FCSTD DOCUMENT  (FreeCAD 1.1R41365 (Git))
Label: Assembly_WireFlexureUnit
License: All rights reserved
LicenseURL: https://en.wikipedia.org/wiki/All_rights_reserved
objects: App::FeaturePython×24, App::Link×16, App::Point×1, Assembly::JointGroup×1, Assembly::AssemblyObject×1
EXTERNAL_REF file=WireFlexure.FCStd obj=Body
EXTERNAL_REF file=BallJointMount.FCStd obj=Body
EXTERNAL_REF file=JointBall.FCStd obj=Body
EXTERNAL_REF file=RubberBandCollet.FCStd obj=Body
EXTERNAL_REF file=RubberBand.FCStd obj=Body

FEATURE [App::Point] Origin001
  Role = Origin
FEATURE [App::Link] FlexureWire  label="FlexureWire1"
  LinkPlacement = pos=(-8.5,9.53674e-07,0) rot=(0,0,1;0rad)
  LinkedObject = -> <external WireFlexure.FCStd>#Body
  Placement = pos=(-8.5,9.53674e-07,0) rot=(0,0,1;0rad)
FEATURE [App::FeaturePython] GroundedJoint  # Assembly grounded joint (typed FeaturePython)
  ObjectToGround = -> FlexureWire
FEATURE [App::Link] FlexureWire001  label="FlexureWire2"
  LinkPlacement = pos=(8.5,-9.53675e-07,0) rot=(0,0,1;0rad)
  LinkedObject = -> <external WireFlexure.FCStd>#Body
  Placement = pos=(8.5,-9.53675e-07,0) rot=(0,0,1;0rad)
FEATURE [App::Link] WireMount  label="WireMount1"
  LinkPlacement = pos=(1.421e-13,40,0) rot=(0,0,1;0rad)
  LinkedObject = -> <external BallJointMount.FCStd>#Body
  Placement = pos=(1.421e-13,40,0) rot=(0,0,1;0rad)
FEATURE [App::Link] WireMount001  label="WireMount2"
  LinkPlacement = pos=(3.73908e-06,-40,0) rot=(1,0,0;3.14159rad)
  LinkedObject = -> <external BallJointMount.FCStd>#Body
  Placement = pos=(3.73908e-06,-40,0) rot=(1,0,0;3.14159rad)
FEATURE [App::Link] Ball  label="Ball1"
  LinkPlacement = pos=(-8.5,36.5,0) rot=(0,0,1;0rad)
  LinkedObject = -> <external JointBall.FCStd>#Body
  Placement = pos=(-8.5,36.5,0) rot=(0,0,1;0rad)
FEATURE [App::Link] Ball001  label="Ball2"
  LinkPlacement = pos=(8.5,36.5,0) rot=(0,0,1;0rad)
  LinkedObject = -> <external JointBall.FCStd>#Body
  Placement = pos=(8.5,36.5,0) rot=(0,0,1;0rad)
FEATURE [App::Link] Ball002  label="Ball3"
  LinkPlacement = pos=(-8.5,-36.5,0) rot=(0,0,1;0rad)
  LinkedObject = -> <external JointBall.FCStd>#Body
  Placement = pos=(-8.5,-36.5,0) rot=(0,0,1;0rad)
FEATURE [App::Link] Ball003  label="Ball4"
  LinkPlacement = pos=(8.5,-36.5,0) rot=(0,0,1;0rad)
  LinkedObject = -> <external JointBall.FCStd>#Body
  Placement = pos=(8.5,-36.5,0) rot=(0,0,1;0rad)
FEATURE [App::FeaturePython] GroundedJoint001  # Assembly grounded joint (typed FeaturePython)
  ObjectToGround = -> FlexureWire001
FEATURE [App::FeaturePython] GroundedJoint002  # Assembly grounded joint (typed FeaturePython)
  ObjectToGround = -> WireMount
FEATURE [App::FeaturePython] GroundedJoint003  # Assembly grounded joint (typed FeaturePython)
  ObjectToGround = -> WireMount001
FEATURE [App::FeaturePython] GroundedJoint004  # Assembly grounded joint (typed FeaturePython)
  ObjectToGround = -> Ball
FEATURE [App::FeaturePython] GroundedJoint005  # Assembly grounded joint (typed FeaturePython)
  ObjectToGround = -> Ball001
FEATURE [App::FeaturePython] GroundedJoint006  # Assembly grounded joint (typed FeaturePython)
  ObjectToGround = -> Ball002
FEATURE [App::FeaturePython] GroundedJoint007  # Assembly grounded joint (typed FeaturePython)
  ObjectToGround = -> Ball003
FEATURE [App::Link] RubberBandCollet
  LinkPlacement = pos=(-8.5,-24,-1.04e-14) rot=(1,0,0;1.5708rad)
  LinkedObject = -> <external RubberBandCollet.FCStd>#Body
  Placement = pos=(-8.5,-24,-1.04e-14) rot=(1,0,0;1.5708rad)
FEATURE [App::Link] RubberBandCollet001
  LinkPlacement = pos=(8.5,-24,-1.04e-14) rot=(1,0,0;1.5708rad)
  LinkedObject = -> <external RubberBandCollet.FCStd>#Body
  Placement = pos=(8.5,-24,-1.04e-14) rot=(1,0,0;1.5708rad)
FEATURE [App::Link] RubberBandCollet002
  LinkPlacement = pos=(-8.5,24,-5.5e-15) rot=(1,0,0;4.71239rad)
  LinkedObject = -> <external RubberBandCollet.FCStd>#Body
  Placement = pos=(-8.5,24,-5.5e-15) rot=(1,0,0;4.71239rad)
FEATURE [App::Link] RubberBandCollet003
  LinkPlacement = pos=(8.5,24,-5.5e-15) rot=(1,0,0;4.71239rad)
  LinkedObject = -> <external RubberBandCollet.FCStd>#Body
  Placement = pos=(8.5,24,-5.5e-15) rot=(1,0,0;4.71239rad)
FEATURE [App::Link] RubberBand
  LinkPlacement = pos=(-8.5,-44,-2.22928e-06) rot=(0,1,0;1.5708rad)
  LinkedObject = -> <external RubberBand.FCStd>#Body
  Placement = pos=(-8.5,-44,-2.22928e-06) rot=(0,1,0;1.5708rad)
FEATURE [App::Link] RubberBand001
  LinkPlacement = pos=(8.5,-44,2.22928e-06) rot=(0,1,0;1.5708rad)
  LinkedObject = -> <external RubberBand.FCStd>#Body
  Placement = pos=(8.5,-44,2.22928e-06) rot=(0,1,0;1.5708rad)
FEATURE [App::Link] RubberBand002
  LinkPlacement = pos=(8.5,44,7e-16) rot=(0.707107,0,-0.707107;3.14159rad)
  LinkedObject = -> <external RubberBand.FCStd>#Body
  Placement = pos=(8.5,44,7e-16) rot=(0.707107,0,-0.707107;3.14159rad)
FEATURE [App::Link] RubberBand003
  LinkPlacement = pos=(-8.5,44,-1.4e-15) rot=(-0.707107,0,0.707107;3.14159rad)
  LinkedObject = -> <external RubberBand.FCStd>#Body
  Placement = pos=(-8.5,44,-1.4e-15) rot=(-0.707107,0,0.707107;3.14159rad)
FEATURE [App::FeaturePython] Joint  label="Fixed002"  # Assembly joint (typed FeaturePython)
  Activated = true
  Angle = 0
  AngleMax = 0
  AngleMin = 0
  Detach1 = false
  Detach2 = false
  Distance = 0
  Distance2 = 0
  EnableAngleMax = false
  EnableAngleMin = false
  EnableLengthMax = false
  EnableLengthMin = false
  JointType = 0 (Fixed)
  LengthMax = 0
  LengthMin = 0
  Offset2 = pos=(0,0,-8) rot=(0,0,1;0rad)
  Placement1 = pos=(0,0,3) rot=(0,0,1;0rad)
  Placement2 = pos=(0,-27,-9.8e-15) rot=(1,0,0;1.5708rad)
  Reference1 = -> Assembly [RubberBandCollet.Face20,RubberBandCollet.Edge3]
  Reference2 = -> Assembly [FlexureWire.Face1,FlexureWire.Edge3]
  Suppressed = false
FEATURE [App::FeaturePython] Joint001  label="Fixed"  # Assembly joint (typed FeaturePython)
  Activated = true
  Angle = 0
  AngleMax = 0
  AngleMin = 0
  Detach1 = false
  Detach2 = false
  Distance = 0
  Distance2 = 0
  EnableAngleMax = false
  EnableAngleMin = false
  EnableLengthMax = false
  EnableLengthMin = false
  JointType = 0 (Fixed)
  LengthMax = 0
  LengthMin = 0
  Offset2 = pos=(0,0,-8) rot=(0,0,1;0rad)
  Placement1 = pos=(0,0,3) rot=(0,0,1;0rad)
  Placement2 = pos=(0,-27,-9.8e-15) rot=(1,0,0;1.5708rad)
  Reference1 = -> Assembly [RubberBandCollet001.Edge27,RubberBandCollet001.Edge27]
  Reference2 = -> Assembly [FlexureWire001.Face1,FlexureWire001.Edge3]
  Suppressed = false
FEATURE [App::FeaturePython] Joint002  label="Fixed003"  # Assembly joint (typed FeaturePython)
  Activated = true
  Angle = 0
  AngleMax = 0
  AngleMin = 0
  Detach1 = false
  Detach2 = false
  Distance = 0
  Distance2 = 0
  EnableAngleMax = false
  EnableAngleMin = false
  EnableLengthMax = false
  EnableLengthMin = false
  JointType = 0 (Fixed)
  LengthMax = 0
  LengthMin = 0
  Offset2 = pos=(0,0,8) rot=(0,0,1;0rad)
  Placement1 = pos=(0,0,3) rot=(0,0,1;0rad)
  Placement2 = pos=(0,27,-6.2e-15) rot=(1,0,0;1.5708rad)
  Reference1 = -> Assembly [RubberBandCollet002.Edge27,RubberBandCollet002.Edge27]
  Reference2 = -> Assembly [FlexureWire.Face1,FlexureWire.Edge2]
  Suppressed = false
FEATURE [App::FeaturePython] Joint003  label="Fixed005"  # Assembly joint (typed FeaturePython)
  Activated = true
  Angle = 0
  AngleMax = 0
  AngleMin = 0
  Detach1 = false
  Detach2 = false
  Distance = 0
  Distance2 = 0
  EnableAngleMax = false
  EnableAngleMin = false
  EnableLengthMax = false
  EnableLengthMin = false
  JointType = 0 (Fixed)
  LengthMax = 0
  LengthMin = 0
  Offset2 = pos=(0,0,8) rot=(0,0,1;0rad)
  Placement1 = pos=(0,0,3) rot=(0,0,1;0rad)
  Placement2 = pos=(0,27,-6.2e-15) rot=(1,0,0;1.5708rad)
  Reference1 = -> Assembly [RubberBandCollet003.Edge27,RubberBandCollet003.Edge27]
  Reference2 = -> Assembly [FlexureWire001.Face1,FlexureWire001.Edge2]
  Suppressed = false
FEATURE [App::FeaturePython] Joint004  label="Cylindrical009"  # Assembly joint (typed FeaturePython)
  Activated = true
  Angle = 0
  AngleMax = 0
  AngleMin = 0
  Detach1 = false
  Detach2 = false
  Distance = 0
  Distance2 = 0
  EnableAngleMax = false
  EnableAngleMin = false
  EnableLengthMax = false
  EnableLengthMin = false
  JointType = 2 (Cylindrical)
  LengthMax = 0
  LengthMin = 0
  Placement1 = pos=(-1.75,0,0) rot=(1,0,0;1.5708rad)
  Placement2 = pos=(-8.5,3,-1.75) rot=(-1,0,0;4.71239rad)
  Reference1 = -> Assembly [RubberBand.Edge1,RubberBand.Edge1]
  Reference2 = -> Assembly [WireMount001.Edge38,WireMount001.Edge38]
  Suppressed = false
FEATURE [App::FeaturePython] Joint005  label="Cylindrical010"  # Assembly joint (typed FeaturePython)
  Activated = true
  Angle = 0
  AngleMax = 0
  AngleMin = 0
  Detach1 = false
  Detach2 = false
  Distance = 0
  Distance2 = 0
  EnableAngleMax = false
  EnableAngleMin = false
  EnableLengthMax = false
  EnableLengthMin = false
  JointType = 2 (Cylindrical)
  LengthMax = 0
  LengthMin = 0
  Placement1 = pos=(1.75,7.1e-15,0) rot=(0,-0.707107,0.707107;3.14159rad)
  Placement2 = pos=(-8.5,3,1.75) rot=(-1,0,0;4.71239rad)
  Reference1 = -> Assembly [RubberBand.Face5,RubberBand.Edge2]
  Reference2 = -> Assembly [WireMount001.Edge37,WireMount001.Edge37]
  Suppressed = false
FEATURE [App::FeaturePython] Joint006  label="Distance007"  # Assembly joint (typed FeaturePython)
  Activated = true
  Angle = 0
  AngleMax = 0
  AngleMin = 0
  Detach1 = false
  Detach2 = false
  Distance = -1
  Distance2 = 0
  EnableAngleMax = false
  EnableAngleMin = false
  EnableLengthMax = false
  EnableLengthMin = false
  JointType = 5 (Distance)
  LengthMax = 0
  LengthMin = 0
  Placement1 = pos=(-1.75,0,0) rot=(0.57735,0.57735,-0.57735;2.0944rad)
  Placement2 = pos=(2.1e-15,3,8e-16) rot=(-0.57735,-0.57735,-0.57735;2.0944rad)
  Reference1 = -> Assembly [RubberBand.Face1,RubberBand.Face1]
  Reference2 = -> Assembly [WireMount001.Face12,WireMount001.Vertex27]
  Suppressed = false
FEATURE [App::FeaturePython] Joint007  label="Cylindrical011"  # Assembly joint (typed FeaturePython)
  Activated = true
  Angle = 0
  AngleMax = 0
  AngleMin = 0
  Detach1 = false
  Detach2 = false
  Distance = 0
  Distance2 = 0
  EnableAngleMax = false
  EnableAngleMin = false
  EnableLengthMax = false
  EnableLengthMin = false
  JointType = 2 (Cylindrical)
  LengthMax = 0
  LengthMin = 0
  Placement1 = pos=(-1.75,-7.1e-15,0) rot=(1,0,0;1.5708rad)
  Placement2 = pos=(8.5,3,-1.75) rot=(0,-0.707107,-0.707107;3.14159rad)
  Reference1 = -> Assembly [RubberBand001.Edge1,RubberBand001.Edge1]
  Reference2 = -> Assembly [WireMount001.Edge40,WireMount001.Edge40]
  Suppressed = false
FEATURE [App::FeaturePython] Joint008  label="Cylindrical012"  # Assembly joint (typed FeaturePython)
  Activated = true
  Angle = 0
  AngleMax = 0
  AngleMin = 0
  Detach1 = false
  Detach2 = false
  Distance = 0
  Distance2 = 0
  EnableAngleMax = false
  EnableAngleMin = false
  EnableLengthMax = false
  EnableLengthMin = false
  JointType = 2 (Cylindrical)
  LengthMax = 0
  LengthMin = 0
  Placement1 = pos=(1.75,0,0) rot=(0,-0.707107,0.707107;3.14159rad)
  Placement2 = pos=(8.5,3,1.75) rot=(0,-0.707107,-0.707107;3.14159rad)
  Reference1 = -> Assembly [RubberBand001.Face5,RubberBand001.Edge2]
  Reference2 = -> Assembly [WireMount001.Face27,WireMount001.Edge3]
  Suppressed = false
FEATURE [App::FeaturePython] Joint009  label="Distance009"  # Assembly joint (typed FeaturePython)
  Activated = true
  Angle = 0
  AngleMax = 0
  AngleMin = 0
  Detach1 = false
  Detach2 = false
  Distance = -1
  Distance2 = 0
  EnableAngleMax = false
  EnableAngleMin = false
  EnableLengthMax = false
  EnableLengthMin = false
  JointType = 5 (Distance)
  LengthMax = 0
  LengthMin = 0
  Placement1 = pos=(-1.75,-7.1e-15,0) rot=(0.57735,0.57735,-0.57735;2.0944rad)
  Placement2 = pos=(2.1e-15,3,8e-16) rot=(-0.57735,-0.57735,-0.57735;2.0944rad)
  Reference1 = -> Assembly [RubberBand001.Face1,RubberBand001.Face1]
  Reference2 = -> Assembly [WireMount001.Face12,WireMount001.Vertex29]
  Suppressed = false
FEATURE [App::FeaturePython] Joint010  label="Cylindrical013"  # Assembly joint (typed FeaturePython)
  Activated = true
  Angle = 0
  AngleMax = 0
  AngleMin = 0
  Detach1 = false
  Detach2 = false
  Distance = 0
  Distance2 = 0
  EnableAngleMax = false
  EnableAngleMin = false
  EnableLengthMax = false
  EnableLengthMin = false
  JointType = 2 (Cylindrical)
  LengthMax = 0
  LengthMin = 0
  Placement1 = pos=(-1.75,0,0) rot=(1,0,0;1.5708rad)
  Placement2 = pos=(-8.5,3,1.75) rot=(1,0,0;1.5708rad)
  Reference1 = -> Assembly [RubberBand003.Edge1,RubberBand003.Edge1]
  Reference2 = -> Assembly [WireMount.Edge37,WireMount.Edge37]
  Suppressed = false
FEATURE [App::FeaturePython] Joint011  label="Cylindrical014"  # Assembly joint (typed FeaturePython)
  Activated = true
  Angle = 0
  AngleMax = 0
  AngleMin = 0
  Detach1 = false
  Detach2 = false
  Distance = 0
  Distance2 = 0
  EnableAngleMax = false
  EnableAngleMin = false
  EnableLengthMax = false
  EnableLengthMin = false
  JointType = 2 (Cylindrical)
  LengthMax = 0
  LengthMin = 0
  Placement1 = pos=(1.75,0,0) rot=(0,0.707107,-0.707107;3.14159rad)
  Placement2 = pos=(-8.5,3,-1.75) rot=(1,0,0;1.5708rad)
  Reference1 = -> Assembly [RubberBand003.Face5,RubberBand003.Edge2]
  Reference2 = -> Assembly [WireMount.Face26,WireMount.Edge3]
  Suppressed = false
FEATURE [App::FeaturePython] Joint012  label="Distance010"  # Assembly joint (typed FeaturePython)
  Activated = true
  Angle = 0
  AngleMax = 0
  AngleMin = 0
  Detach1 = false
  Detach2 = false
  Distance = -1
  Distance2 = 0
  EnableAngleMax = false
  EnableAngleMin = false
  EnableLengthMax = false
  EnableLengthMin = false
  JointType = 5 (Distance)
  LengthMax = 0
  LengthMin = 0
  Placement1 = pos=(-1.75,0,0) rot=(0.57735,0.57735,-0.57735;2.0944rad)
  Placement2 = pos=(1.5e-15,3,8e-16) rot=(0.57735,0.57735,0.57735;4.18879rad)
  Reference1 = -> Assembly [RubberBand003.Face1,RubberBand003.Face1]
  Reference2 = -> Assembly [WireMount.Face12,WireMount.Vertex26]
  Suppressed = false
FEATURE [App::FeaturePython] Joint013  label="Cylindrical015"  # Assembly joint (typed FeaturePython)
  Activated = true
  Angle = 0
  AngleMax = 0
  AngleMin = 0
  Detach1 = false
  Detach2 = false
  Distance = 0
  Distance2 = 0
  EnableAngleMax = false
  EnableAngleMin = false
  EnableLengthMax = false
  EnableLengthMin = false
  JointType = 2 (Cylindrical)
  LengthMax = 0
  LengthMin = 0
  Placement1 = pos=(-1.75,0,0) rot=(1,0,0;1.5708rad)
  Placement2 = pos=(8.5,3,1.75) rot=(0,0.707107,0.707107;3.14159rad)
  Reference1 = -> Assembly [RubberBand002.Edge1,RubberBand002.Edge1]
  Reference2 = -> Assembly [WireMount.Edge39,WireMount.Edge39]
  Suppressed = false
FEATURE [App::FeaturePython] Joint014  label="Cylindrical018"  # Assembly joint (typed FeaturePython)
  Activated = true
  Angle = 0
  AngleMax = 0
  AngleMin = 0
  Detach1 = false
  Detach2 = false
  Distance = 0
  Distance2 = 0
  EnableAngleMax = false
  EnableAngleMin = false
  EnableLengthMax = false
  EnableLengthMin = false
  JointType = 2 (Cylindrical)
  LengthMax = 0
  LengthMin = 0
  Placement1 = pos=(1.75,0,0) rot=(0,-0.707107,0.707107;3.14159rad)
  Placement2 = pos=(8.5,3,-1.75) rot=(0,0.707107,0.707107;3.14159rad)
  Reference1 = -> Assembly [RubberBand002.Face5,RubberBand002.Edge2]
  Reference2 = -> Assembly [WireMount.Face28,WireMount.Edge3]
  Suppressed = false
FEATURE [App::FeaturePython] Joint015  label="Distance014"  # Assembly joint (typed FeaturePython)
  Activated = true
  Angle = 0
  AngleMax = 0
  AngleMin = 0
  Detach1 = false
  Detach2 = false
  Distance = -1
  Distance2 = 0
  EnableAngleMax = false
  EnableAngleMin = false
  EnableLengthMax = false
  EnableLengthMin = false
  JointType = 5 (Distance)
  LengthMax = 0
  LengthMin = 0
  Placement1 = pos=(-1.75,0,0) rot=(-0.57735,-0.57735,0.57735;4.18879rad)
  Placement2 = pos=(1.5e-15,3,8e-16) rot=(0.57735,0.57735,0.57735;4.18879rad)
  Reference1 = -> Assembly [RubberBand002.Face1,RubberBand002.Face1]
  Reference2 = -> Assembly [WireMount.Face12,WireMount.Face12]
  Suppressed = false
FEATURE [Assembly::JointGroup] Joints
  Group = -> [GroundedJoint,GroundedJoint001,GroundedJoint002,GroundedJoint003,GroundedJoint004,GroundedJoint005,GroundedJoint006,GroundedJoint007,Joint,Joint001,Joint002,Joint003,Joint004,Joint005,Joint006,Joint007,Joint008,Joint009,Joint010,Joint011,Joint012,Joint013,Joint014,Joint015]
FEATURE [Assembly::AssemblyObject] Assembly  label="WireFlexureUnit"
  Group = -> [Joints,FlexureWire,GroundedJoint,FlexureWire001,WireMount,WireMount001,Ball,Ball001,Ball002,Ball003,GroundedJoint001,GroundedJoint002,GroundedJoint003,GroundedJoint004,GroundedJoint005,GroundedJoint006,GroundedJoint007,RubberBandCollet,RubberBandCollet001,RubberBandCollet002,RubberBandCollet003,RubberBand,RubberBand001,RubberBand002,RubberBand003,Joint,Joint001,Joint002,Joint003,Joint004,Joint005,+10 more]
  Origin = -> Origin
  Type = Assembly

RESOLVED EXTERNAL PARTS (link-assembly join: the EXTERNAL_REF files above that resolve inside this repo's crawl, each included once):
---- part BallJointMount.FCStd = doc fcstd_7bda6f26d7a0 ----
FCSTD DOCUMENT  (FreeCAD 1.1R41365 (Git))
Label: BallJointMount
License: All rights reserved
LicenseURL: https://en.wikipedia.org/wiki/All_rights_reserved
objects: Sketcher::SketchObject×4, PartDesign::Pocket×3, PartDesign::Chamfer×2, App::Point×1, PartDesign::Pad×1, PartDesign::Fillet×1, PartDesign::Mirrored×1, PartDesign::Body×1
note: 32 computed .brp shape members not serialized (recipe doc carries the construction recipe); baked Part::Feature solids carry a one-line shape summary decoded from their .brp

FEATURE [App::Point] Origin001
  Role = Origin
FEATURE [Sketcher::SketchObject] Sketch
  ArcFitTolerance = 1e-06
  AttachmentSupport = -> [XY_Plane]
  ExternalTypes = [0]
  FullyConstrained = true
  MakeInternals = false
  MapMode = 5
  sketch-geometry (5):
    g0: LineSegment StartX=-10 StartY=-3 StartZ=0 EndX=0 EndY=-3 EndZ=0
    g1: LineSegment StartX=0 StartY=-3 StartZ=0 EndX=0 EndY=3 EndZ=0
    g2: LineSegment StartX=0 StartY=3 StartZ=0 EndX=-10 EndY=3 EndZ=0
    g3: GeomPoint [constr] X=0 Y=0 Z=0
    g4: LineSegment StartX=-10 StartY=3 StartZ=0 EndX=-10 EndY=-3 EndZ=0
  constraints (12):
    c: Coincident(g0,g1)
    c: Coincident(g1,g2)
    c: Horizontal(g0)
    c: Horizontal(g2)
    c: Vertical(g1)
    c: Coincident(g3,g-1)
    c: DistanceX(g0,g0) = 10
    c: DistanceY(g1,g1) = 6
    c: Symmetric(g1,g1,g3)
    c: Coincident(g4,g2)
    c: Coincident(g4,g0)
    c: Vertical(g4)
FEATURE [PartDesign::Pad] Pad
  Direction = (0,0,1)
  Length = 6
  Length2 = 10
  Midplane = true
  Profile = -> Sketch
  ReferenceAxis = -> Sketch [N_Axis]
  Refine = true
  Suppressed = false
  Type = 0
FEATURE [Sketcher::SketchObject] Sketch001
  ArcFitTolerance = 1e-06
  AttachmentSupport = -> [Pad]
  ExternalTypes = [0]
  FullyConstrained = true
  MakeInternals = false
  MapMode = 5
  Placement = pos=(0,0,3) rot=(0,0,1;0rad)
  sketch-geometry (1):
    g0: Circle CenterX=-5 CenterY=0 CenterZ=0 NormalX=0 NormalY=0 NormalZ=1 AngleXU=0 Radius=1.1
  constraints (3):
    c: Diameter(g0) = 2.2
    c: DistanceX(g0,g-1) = 5
    c: PointOnObject(g0,g-1)
FEATURE [PartDesign::Pocket] Pocket
  BaseFeature = -> Pad
  Direction = (0,0,-1)
  Length = 5
  Length2 = 5
  Profile = -> Sketch001
  ReferenceAxis = -> Sketch001 [N_Axis]
  Refine = true
  Suppressed = false
  Type = 1
FEATURE [Sketcher::SketchObject] Sketch002
  ArcFitTolerance = 1e-06
  AttachmentSupport = -> [Pocket]
  ExternalTypes = [0]
  FullyConstrained = true
  MakeInternals = false
  MapMode = 5
  Placement = pos=(0,-3,0) rot=(1,0,0;1.5708rad)
  sketch-geometry (1):
    g0: Circle CenterX=-8.5 CenterY=0 CenterZ=0 NormalX=0 NormalY=0 NormalZ=1 AngleXU=0 Radius=0.5
  constraints (3):
    c: Diameter(g0) = 1
    c: DistanceX(g0,g-1) = 8.5
    c: PointOnObject(g0,g-1)
FEATURE [PartDesign::Pocket] Pocket001
  BaseFeature = -> Pocket
  Direction = (0,1,-2e-16)
  Length = 1
  Length2 = 5
  Profile = -> Sketch002
  ReferenceAxis = -> Sketch002 [N_Axis]
  Refine = true
  Suppressed = false
  Type = 0
FEATURE [PartDesign::Chamfer] Chamfer
  Angle = 45
  Base = -> Pocket001 [Edge14]
  BaseFeature = -> Pocket001
  ChamferType = 0
  FlipDirection = false
  Refine = true
  Size = 1.2
  Size2 = 1
  SupportTransform = false
  Suppressed = false
  UseAllEdges = false
FEATURE [Sketcher::SketchObject] Sketch004
  ArcFitTolerance = 1e-06
  AttachmentSupport = -> [Chamfer]
  ExternalGeometry = -> [Chamfer]
  ExternalTypes = [0]
  FullyConstrained = true
  MakeInternals = false
  MapMode = 5
  Placement = pos=(0,-3,0) rot=(1,0,0;1.5708rad)
  sketch-geometry (3):
    g0: Circle CenterX=-8.5 CenterY=1.75 CenterZ=0 NormalX=0 NormalY=0 NormalZ=1 AngleXU=0 Radius=0.6
    g1: Circle CenterX=-8.5 CenterY=-1.75 CenterZ=0 NormalX=0 NormalY=0 NormalZ=1 AngleXU=0 Radius=0.6
    g2: LineSegment [constr] StartX=-8.5 StartY=1.75 StartZ=0 EndX=-8.5 EndY=-1.75 EndZ=0
  constraints (7):
    c: Diameter(g0) = 1.2
    c: Equal(g0,g1)
    c: Coincident(g2,g0)
    c: Coincident(g2,g1)
    c: Symmetric(g2,g2,g-3)
    c: Distance(g2,g2) = 3.5
    c: Vertical(g2)
FEATURE [PartDesign::Pocket] Pocket002
  BaseFeature = -> Chamfer
  Direction = (0,1,-2e-16)
  Length = 5
  Length2 = 5
  Profile = -> Sketch004
  ReferenceAxis = -> Sketch004 [N_Axis]
  Refine = true
  Suppressed = false
  Type = 1
FEATURE [PartDesign::Fillet] Fillet
  Base = -> Pocket002 [Edge3,Edge15]
  BaseFeature = -> Pocket002
  Radius = 0.5
  Refine = true
  SupportTransform = false
  Suppressed = false
  UseAllEdges = false
FEATURE [PartDesign::Mirrored] Mirrored
  BaseFeature = -> Fillet
  MirrorPlane = -> YZ_Plane
  Refine = true
  Suppressed = false
  TransformMode = 1
FEATURE [PartDesign::Chamfer] Chamfer001
  Angle = 45
  Base = -> Mirrored [Edge5,Edge11]
  BaseFeature = -> Mirrored
  ChamferType = 0
  FlipDirection = false
  Refine = true
  Size = 0.2
  Size2 = 1
  SupportTransform = false
  Suppressed = false
  UseAllEdges = false
FEATURE [PartDesign::Body] Body  label="BallJointMount"
  AllowCompound = false
  Group = -> [Sketch,Pad,Sketch001,Pocket,Sketch002,Pocket001,Chamfer,Sketch004,Pocket002,Fillet,Mirrored,Chamfer001]
  Origin = -> Origin
  Tip = -> Chamfer001
---- part JointBall.FCStd = doc fcstd_40ae3ec74856 ----
FCSTD DOCUMENT  (FreeCAD 1.1R41365 (Git))
Label: JointBall
License: All rights reserved
LicenseURL: https://en.wikipedia.org/wiki/All_rights_reserved
objects: App::Point×1, Sketcher::SketchObject×1, PartDesign::Revolution×1, PartDesign::Body×1
note: 6 computed .brp shape members not serialized (recipe doc carries the construction recipe); baked Part::Feature solids carry a one-line shape summary decoded from their .brp

FEATURE [App::Point] Origin001
  Role = Origin
FEATURE [Sketcher::SketchObject] Sketch
  ArcFitTolerance = 1e-06
  AttachmentSupport = -> [Origin]
  ExternalTypes = [0]
  FullyConstrained = false
  MakeInternals = false
  MapMode = 5
  sketch-geometry (2):
    g0: ArcOfCircle CenterX=0.0245252 CenterY=-0.048148 CenterZ=0 NormalX=0 NormalY=0 NormalZ=1 AngleXU=0 Radius=0.75 StartAngle=0.0642415 EndAngle=3.07735
    g1: LineSegment StartX=-0.723928 StartY=0 StartZ=0 EndX=0.772978 EndY=0 EndZ=0
  constraints (5):
    c: Coincident(g1,g0)
    c: Coincident(g1,g0)
    c: Horizontal(g1)
    c: Radius(g0) = 0.75
    c: PointOnObject(g0,g-1)
FEATURE [PartDesign::Revolution] Revolution
  Angle = 360
  Angle2 = 60
  Axis = (1,0,0)
  Base = (0,0,0)
  Profile = -> Sketch
  ReferenceAxis = -> Sketch [H_Axis]
  Refine = true
  Suppressed = false
  Type = 0
FEATURE [PartDesign::Body] Body  label="Ball"
  AllowCompound = false
  Group = -> [Sketch,Revolution]
  Origin = -> Origin
  Tip = -> Revolution
---- part RubberBand.FCStd = doc fcstd_05857427589b ----
FCSTD DOCUMENT  (FreeCAD 1.1R41365 (Git))
Label: RubberBand
License: All rights reserved
LicenseURL: https://en.wikipedia.org/wiki/All_rights_reserved
objects: Sketcher::SketchObject×2, App::Point×1, PartDesign::AdditivePipe×1, PartDesign::Mirrored×1, PartDesign::Body×1
note: 10 computed .brp shape members not serialized (recipe doc carries the construction recipe); baked Part::Feature solids carry a one-line shape summary decoded from their .brp

FEATURE [App::Point] Origin001
  Role = Origin
FEATURE [Sketcher::SketchObject] Sketch
  ArcFitTolerance = 1e-06
  AttachmentSupport = -> [Origin]
  ExternalTypes = [0]
  FullyConstrained = true
  MakeInternals = false
  MapMode = 5
  sketch-geometry (2):
    g0: LineSegment StartX=-1.75 StartY=0 StartZ=0 EndX=-1.75 EndY=20 EndZ=0
    g1: ArcOfCircle CenterX=0 CenterY=20 CenterZ=0 NormalX=0 NormalY=0 NormalZ=1 AngleXU=0 Radius=1.75 StartAngle=1.5708 EndAngle=3.14159
  constraints (7):
    c: PointOnObject(g0,g-1)
    c: Vertical(g0)
    c: PointOnObject(g1,g-2)
    c: PointOnObject(g1,g-2)
    c: Tangent(g1,g0) = 1.5708
    c: Distance(g-1,g0) = 1.75
    c: DistanceY(g0,g0) = 20
FEATURE [Sketcher::SketchObject] Sketch001
  ArcFitTolerance = 1e-06
  AttachmentSupport = -> [Origin]
  ExternalGeometry = -> [Sketch]
  ExternalTypes = [0]
  FullyConstrained = true
  MakeInternals = false
  MapMode = 5
  Placement = pos=(0,0,0) rot=(1,0,0;1.5708rad)
  sketch-geometry (1):
    g0: Circle CenterX=-1.75 CenterY=0 CenterZ=0 NormalX=0 NormalY=0 NormalZ=1 AngleXU=0 Radius=0.5
  constraints (2):
    c: Diameter(g0) = 1
    c: Coincident(g0,g-3)
FEATURE [PartDesign::AdditivePipe] AdditivePipe
  AuxiliaryCurvilinear = true
  AuxiliarySpineTangent = false
  Binormal = (0,0,0)
  Mode = 0
  Profile = -> Sketch001
  Refine = true
  Spine = -> Sketch
  SpineTangent = false
  Suppressed = false
  Transformation = 0
  Transition = 0
FEATURE [PartDesign::Mirrored] Mirrored
  BaseFeature = -> AdditivePipe
  MirrorPlane = -> YZ_Plane
  Refine = true
  Suppressed = false
  TransformMode = 1
FEATURE [PartDesign::Body] Body  label="RubberBand"
  AllowCompound = false
  Group = -> [Sketch,Sketch001,AdditivePipe,Mirrored]
  Origin = -> Origin
  Tip = -> Mirrored
---- part RubberBandCollet.FCStd = doc fcstd_46be4b665b96 ----
FCSTD DOCUMENT  (FreeCAD 1.1R41365 (Git))
Label: RubberBandCollet
License: All rights reserved
LicenseURL: https://en.wikipedia.org/wiki/All_rights_reserved
objects: Sketcher::SketchObject×2, App::Point×1, PartDesign::Pad×1, PartDesign::Pocket×1, PartDesign::PolarPattern×1, PartDesign::Chamfer×1, PartDesign::Body×1
note: 16 computed .brp shape members not serialized (recipe doc carries the construction recipe); baked Part::Feature solids carry a one-line shape summary decoded from their .brp

FEATURE [App::Point] Origin001
  Role = Origin
FEATURE [Sketcher::SketchObject] Sketch
  ArcFitTolerance = 1e-06
  AttachmentSupport = -> [Origin]
  ExternalTypes = [0]
  FullyConstrained = true
  MakeInternals = false
  MapMode = 5
  sketch-geometry (8):
    g0: Circle CenterX=0 CenterY=0 CenterZ=0 NormalX=0 NormalY=0 NormalZ=1 AngleXU=0 Radius=1
    g1: ArcOfCircle CenterX=0 CenterY=1 CenterZ=0 NormalX=0 NormalY=0 NormalZ=1 AngleXU=0 Radius=2 StartAngle=2e-16 EndAngle=3.14159
    g2: ArcOfCircle CenterX=0 CenterY=-1 CenterZ=0 NormalX=0 NormalY=0 NormalZ=1 AngleXU=0 Radius=2 StartAngle=3.14159 EndAngle=6.28319
    g3: LineSegment StartX=2 StartY=1 StartZ=0 EndX=2 EndY=-1 EndZ=0
    g4: LineSegment StartX=-2 StartY=1 StartZ=0 EndX=-2 EndY=-1 EndZ=0
    g5: LineSegment [constr] StartX=0 StartY=1 StartZ=0 EndX=0 EndY=-1 EndZ=0
    g6: GeomPoint [constr] X=0 Y=-3 Z=0
    g7: GeomPoint [constr] X=0 Y=3 Z=0
  constraints (17):
    c: Coincident(g0,g-1)
    c: Diameter(g0) = 2
    c: Tangent(g1,g3) = 1.5708
    c: Tangent(g1,g4) = -1.5708
    c: Tangent(g2,g3) = 1.5708
    c: Tangent(g2,g4) = -1.5708
    c: Equal(g1,g2)
    c: Vertical(g4)
    c: Coincident(g5,g1)
    c: Coincident(g5,g2)
    c: Symmetric(g5,g5,g0)
    c: Distance(g3,g4) = 4
    c: PointOnObject(g6,g2)
    c: PointOnObject(g6,g-2)
    c: PointOnObject(g7,g1)
    c: PointOnObject(g7,g-2)
    c: DistanceY(g6,g7) = 6
FEATURE [PartDesign::Pad] Pad
  Direction = (0,0,1)
  Length = 3
  Length2 = 10
  Profile = -> Sketch
  ReferenceAxis = -> Sketch [N_Axis]
  Refine = true
  Suppressed = false
  Type = 0
FEATURE [Sketcher::SketchObject] Sketch001
  ArcFitTolerance = 1e-06
  AttachmentSupport = -> [Pad]
  ExternalTypes = [0]
  FullyConstrained = true
  MakeInternals = false
  MapMode = 5
  Placement = pos=(0,0,3) rot=(0,0,1;0rad)
  sketch-geometry (5):
    g0: ArcOfCircle CenterX=0 CenterY=2 CenterZ=0 NormalX=0 NormalY=0 NormalZ=1 AngleXU=0 Radius=0.5 StartAngle=2.41886 EndAngle=7.00592
    g1: GeomPoint [constr] X=0 Y=3 Z=0
    g2: LineSegment StartX=-0.375 StartY=2.33072 StartZ=0 EndX=-0.375 EndY=4.33072 EndZ=0
    g3: LineSegment StartX=-0.375 StartY=4.33072 StartZ=0 EndX=0.375 EndY=4.33072 EndZ=0
    g4: LineSegment StartX=0.375 StartY=4.33072 StartZ=0 EndX=0.375 EndY=2.33072 EndZ=0
  constraints (15):
    c: PointOnObject(g0,g-2)
    c: PointOnObject(g1,g-3)
    c: PointOnObject(g1,g-2)
    c: Vertical(g2)
    c: Horizontal(g3)
    c: Vertical(g4)
    c: Horizontal(g4,g2)
    c: Coincident(g2,g3)
    c: Coincident(g3,g4)
    c: DistanceX(g3,g3) = 0.75
    c: Diameter(g0) = 1
    c: Coincident(g2,g0)
    c: Coincident(g4,g0)
    c: DistanceY(g4,g4) = 2
    c: DistanceY(g-1,g0) = 2
FEATURE [PartDesign::Pocket] Pocket
  BaseFeature = -> Pad
  Direction = (0,0,-1)
  Length = 5
  Length2 = 5
  Profile = -> Sketch001
  ReferenceAxis = -> Sketch001 [N_Axis]
  Refine = true
  Suppressed = false
  Type = 1
FEATURE [PartDesign::PolarPattern] PolarPattern
  Angle = 360
  Axis = -> Z_Axis
  BaseFeature = -> Pocket
  Mode = 0
  Occurrences = 2
  Offset = 120
  Originals = -> [Pocket]
  Refine = true
  Suppressed = false
  TransformMode = 0
FEATURE [PartDesign::Chamfer] Chamfer
  Angle = 45
  Base = -> PolarPattern [Edge11,Edge25,Edge5,Edge19]
  BaseFeature = -> PolarPattern
  ChamferType = 0
  FlipDirection = false
  Refine = true
  Size = 0.4
  Size2 = 1
  SupportTransform = false
  Suppressed = false
  UseAllEdges = false
FEATURE [PartDesign::Body] Body  label="RubberBandCollet"
  AllowCompound = false
  Group = -> [Sketch,Pad,Sketch001,Pocket,PolarPattern,Chamfer]
  Origin = -> Origin
  Tip = -> Chamfer
---- part WireFlexure.FCStd = doc fcstd_6be79ddcf241 ----
FCSTD DOCUMENT  (FreeCAD 1.1R41365 (Git))
Label: WireFlexure
License: All rights reserved
LicenseURL: https://en.wikipedia.org/wiki/All_rights_reserved
objects: App::Point×1, Sketcher::SketchObject×1, PartDesign::Pad×1, PartDesign::Chamfer×1, PartDesign::Body×1
note: 9 computed .brp shape members not serialized (recipe doc carries the construction recipe); baked Part::Feature solids carry a one-line shape summary decoded from their .brp

FEATURE [App::Point] Origin001
  Role = Origin
FEATURE [Sketcher::SketchObject] Sketch
  ArcFitTolerance = 1e-06
  AttachmentSupport = -> [XZ_Plane]
  ExternalTypes = [0]
  FullyConstrained = true
  MakeInternals = false
  MapMode = 5
  Placement = pos=(0,0,0) rot=(1,0,0;1.5708rad)
  sketch-geometry (1):
    g0: Circle CenterX=0 CenterY=0 CenterZ=0 NormalX=0 NormalY=0 NormalZ=1 AngleXU=0 Radius=1
  constraints (2):
    c: Coincident(g0,g-1)
    c: Diameter(g0) = 2
FEATURE [PartDesign::Pad] Pad
  Direction = (0,-1,0)
  Length = 72
  Length2 = 10
  Midplane = true
  Placement = pos=(0,0,0) rot=(1,0,0;1.5708rad)
  Profile = -> Sketch
  ReferenceAxis = -> Sketch [N_Axis]
  Refine = true
  Suppressed = false
  Type = 0
FEATURE [PartDesign::Chamfer] Chamfer
  Angle = 45
  Base = -> Pad [Edge3,Edge2]
  BaseFeature = -> Pad
  ChamferType = 1
  FlipDirection = false
  Placement = pos=(0,0,0) rot=(1,0,0;1.5708rad)
  Refine = true
  Size = 1
  Size2 = 0.4
  SupportTransform = false
  Suppressed = false
  UseAllEdges = false
FEATURE [PartDesign::Body] Body  label="FlexureWire"
  AllowCompound = false
  Group = -> [Sketch,Pad,Chamfer]
  Origin = -> Origin
  Tip = -> Chamfer
